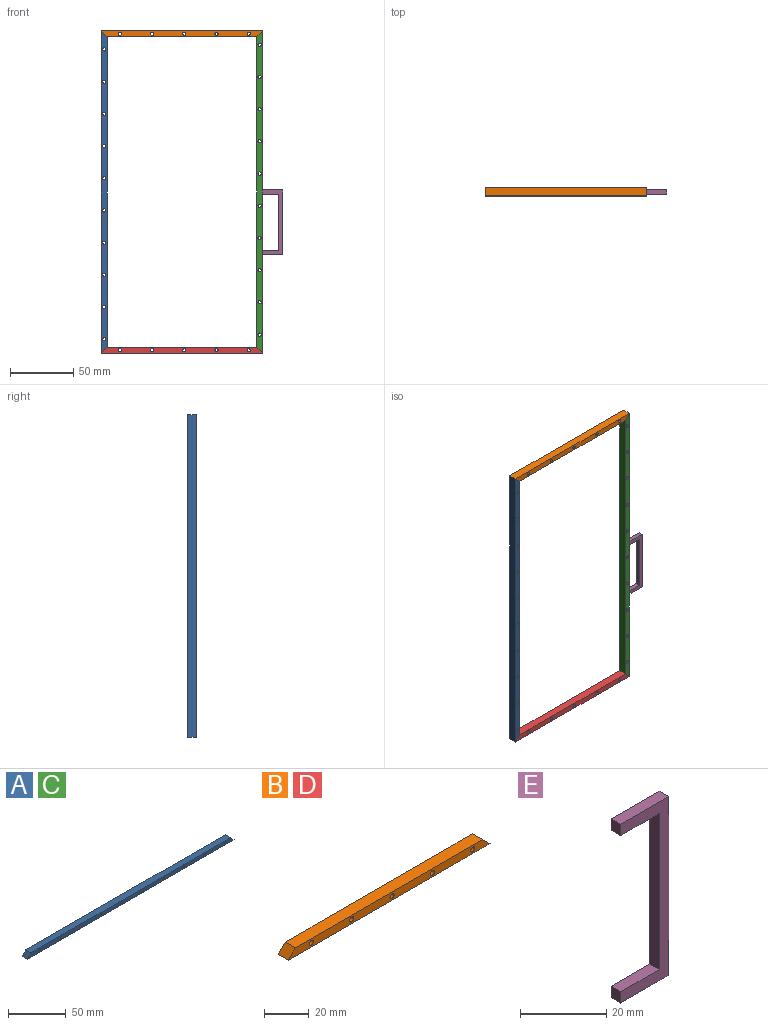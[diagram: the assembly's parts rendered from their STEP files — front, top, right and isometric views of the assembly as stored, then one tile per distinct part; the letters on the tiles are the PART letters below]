
ASSEMBLY  parts=5 mates=4
PART A: 16 faces, bbox 254x6.4x4.5 mm
  f0: cylinder r=1.27mm len=6.35mm, axis (0,-1,0), area 50.7mm2, adj f13,f14
  f1: cylinder r=1.27mm len=6.35mm, axis (0,-1,0), area 50.7mm2, adj f13,f14
  f2: cylinder r=1.27mm len=6.35mm, axis (0,-1,0), area 50.7mm2, adj f13,f14
  f3: cylinder r=1.27mm len=6.35mm, axis (0,-1,0), area 50.7mm2, adj f13,f14
  f4: cylinder r=1.27mm len=6.35mm, axis (0,-1,0), area 50.7mm2, adj f13,f14
  f5: cylinder r=1.27mm len=6.35mm, axis (0,-1,0), area 50.7mm2, adj f13,f14
  f6: cylinder r=1.27mm len=6.35mm, axis (0,-1,0), area 50.7mm2, adj f13,f14
  f7: cylinder r=1.27mm len=6.35mm, axis (0,-1,0), area 50.7mm2, adj f13,f14
  f8: cylinder r=1.27mm len=6.35mm, axis (0,-1,0), area 50.7mm2, adj f13,f14
  f9: plane 6.35x4.49mm, normal (-0.71,0,0.71), area 40.3mm2, adj f10,f12,f13,f14
  f10: plane 254x6.35mm, normal (0,0,-1), area 1612.9mm2, adj f9,f11,f13,f14
  f11: plane 6.35x4.49mm, normal (0.71,0,0.71), area 40.3mm2, adj f10,f12,f13,f14
  f12: plane 245.02x6.35mm, normal (0,0,1), area 1555.9mm2, adj f9,f11,f13,f14
  f13: plane 254x4.49mm, normal (0,-1,0), area 1069.7mm2, adj f0,f1,f2,f3,f4,f5,f6,f7
  f14: plane 254x4.49mm, normal (0,1,0), area 1069.7mm2, adj f0,f1,f2,f3,f4,f5,f6,f7
  f15: cylinder r=1.27mm len=6.35mm, axis (0,-1,0), area 50.7mm2, adj f13,f14
PART B: 11 faces, bbox 127x6.4x4.5 mm
  f0: cylinder r=1.27mm len=6.35mm, axis (0,-1,0), area 50.7mm2, adj f8,f9
  f1: cylinder r=1.27mm len=6.35mm, axis (0,-1,0), area 50.7mm2, adj f8,f9
  f2: cylinder r=1.27mm len=6.35mm, axis (0,-1,0), area 50.7mm2, adj f8,f9
  f3: cylinder r=1.27mm len=6.35mm, axis (0,-1,0), area 50.7mm2, adj f8,f9
  f4: plane 6.35x4.49mm, normal (-0.71,0,0.71), area 40.3mm2, adj f5,f7,f8,f9
  f5: plane 127x6.35mm, normal (0,0,-1), area 806.5mm2, adj f4,f6,f8,f9
  f6: plane 6.35x4.49mm, normal (0.71,0,0.71), area 40.3mm2, adj f5,f7,f8,f9
  f7: plane 118.02x6.35mm, normal (0,0,1), area 749.4mm2, adj f4,f6,f8,f9
  f8: plane 127x4.49mm, normal (0,-1,0), area 524.7mm2, adj f0,f1,f2,f3,f4,f5,f6,f7
  f9: plane 127x4.49mm, normal (0,1,0), area 524.7mm2, adj f0,f1,f2,f3,f4,f5,f6,f7
  f10: cylinder r=1.27mm len=6.35mm, axis (0,-1,0), area 50.7mm2, adj f8,f9
PART C: same geometry as A
PART D: same geometry as B
PART E: 10 faces, bbox 15.9x3.2x50.8 mm
  f0: plane 12.7x3.18mm, normal (0,0,-1), area 40.3mm2, adj f1,f7,f8,f9
  f1: plane 44.45x3.18mm, normal (-1,0,0), area 141.1mm2, adj f0,f2,f8,f9
  f2: plane 12.7x3.18mm, normal (0,0,1), area 40.3mm2, adj f1,f3,f8,f9
  f3: plane 3.18x3.18mm, normal (-1,0,0), area 10.1mm2, adj f2,f4,f8,f9
  f4: plane 15.88x3.18mm, normal (0,0,-1), area 50.4mm2, adj f3,f5,f8,f9
  f5: plane 50.8x3.18mm, normal (1,0,0), area 161.3mm2, adj f4,f6,f8,f9
  f6: plane 15.88x3.18mm, normal (0,0,1), area 50.4mm2, adj f5,f7,f8,f9
  f7: plane 3.18x3.18mm, normal (-1,0,0), area 10.1mm2, adj f0,f6,f8,f9
  f8: plane 50.8x15.88mm, normal (0,-1,0), area 241.9mm2, adj f0,f1,f2,f3,f4,f5,f6,f7
  f9: plane 50.8x15.88mm, normal (0,1,0), area 241.9mm2, adj f0,f1,f2,f3,f4,f5,f6,f7
PLACE A rot(axis=(0,1,0),90deg) t=(-151.78,10.47,221.07)mm
PLACE B rot(axis=(-1,0,0),180deg) t=(-88.28,4.12,284.57)mm
PLACE C rot(axis=(0,-1,0),90deg) t=(-24.78,10.47,94.07)mm
PLACE D rot(axis=(0.93,0.36,0),0deg) t=(-88.28,10.47,30.57)mm
PLACE E t=(-24.78,7.29,133.76)mm
MATE fastened C.f9 <-> D.f6  axis (-0.71,0,-0.71) through (-27.02,7.29,32.82)mm
MATE fastened E.f7 <-> C.f10  axis (-1,0,0) through (-24.78,7.29,157.57)mm
MATE fastened A.f11 <-> D.f4  axis (0.71,0,-0.71) through (-149.53,7.29,32.82)mm
MATE fastened B.f4 <-> A.f9  axis (-0.71,0,-0.71) through (-149.53,7.29,282.33)mm
